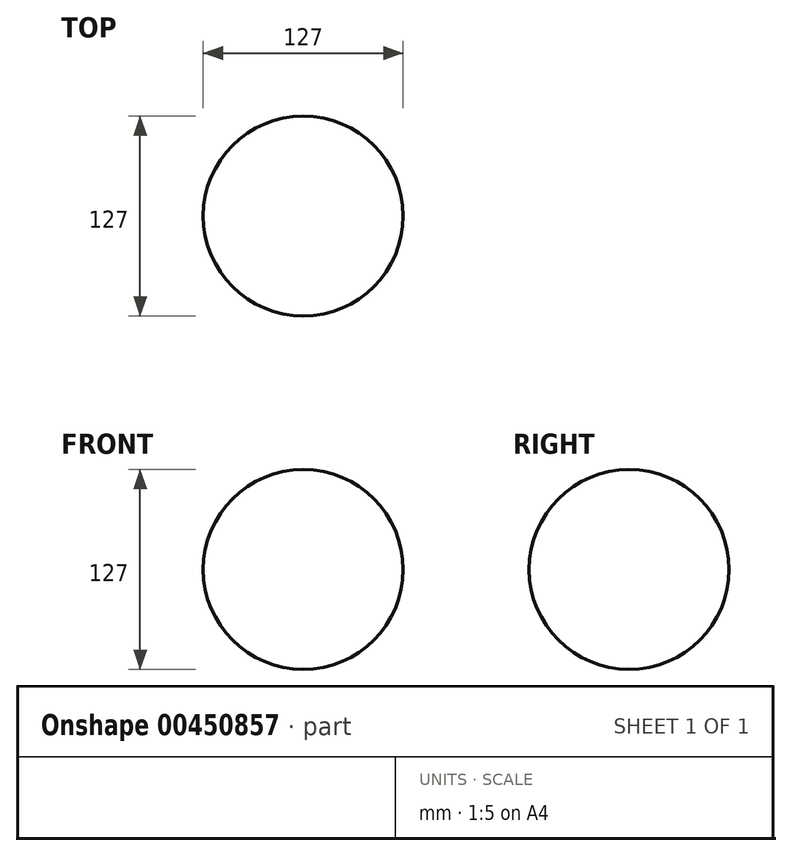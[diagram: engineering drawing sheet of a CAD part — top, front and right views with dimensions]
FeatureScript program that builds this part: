
annotation { "Feature Type Name" : "Feature", "Feature Type Description" : "" }
export const myFeature = defineFeature(function(context is Context, id is Id, definition is map)
    precondition{}
    {
        {
            var Q0;
            Q0=qCreatedBy(makeId("Right.planeOp"),FACE);
            var sketch = newSketch(context, id + "F0", { "sketchPlane" : qUnion([Q0])});
            skCircle(sketch, "E0", {"center": v(0, 0) * mm, "radius": 63.5 * mm});
            skLineSegment(sketch, "E1.bottom", {"start": v(-25.4, -93.12) * mm, "end": v(-38.1, -93.12) * mm});
            skLineSegment(sketch, "E1.top", {"start": v(-25.4, -58.2) * mm, "end": v(-38.1, -58.2) * mm});
            skLineSegment(sketch, "E1.left", {"start": v(-25.4, -93.12) * mm, "end": v(-25.4, -58.2) * mm});
            skLineSegment(sketch, "E1.right", {"start": v(-38.1, -93.12) * mm, "end": v(-38.1, -58.2) * mm});
            skLineSegment(sketch, "E2.MirrorCS", {"start": v(38.1, -93.12) * mm, "end": v(38.1, -58.2) * mm});
            skLineSegment(sketch, "E3.MirrorCS", {"start": v(25.4, -93.12) * mm, "end": v(25.4, -58.2) * mm});
            skLineSegment(sketch, "E4.MirrorCS", {"start": v(25.4, -93.12) * mm, "end": v(38.1, -93.12) * mm});
            skLineSegment(sketch, "E5.MirrorCS", {"start": v(25.4, -58.2) * mm, "end": v(38.1, -58.2) * mm});
            skLineSegment(sketch, "E6.bottom", {"start": v(-38.1, -93.12) * mm, "end": v(-50.8, -93.12) * mm});
            skLineSegment(sketch, "E6.top", {"start": v(-38.1, -50.8) * mm, "end": v(-50.8, -50.8) * mm});
            skLineSegment(sketch, "E6.left", {"start": v(-38.1, -93.12) * mm, "end": v(-38.1, -50.8) * mm});
            skLineSegment(sketch, "E6.right", {"start": v(-50.8, -93.12) * mm, "end": v(-50.8, -50.8) * mm});
            skLineSegment(sketch, "E7.MirrorCS", {"start": v(38.1, -93.12) * mm, "end": v(50.8, -93.12) * mm});
            skLineSegment(sketch, "E8.MirrorCS", {"start": v(50.8, -93.12) * mm, "end": v(50.8, -50.8) * mm});
            skLineSegment(sketch, "E9.MirrorCS", {"start": v(38.1, -93.12) * mm, "end": v(38.1, -50.8) * mm});
            skLineSegment(sketch, "E10.MirrorCS", {"start": v(38.1, -50.8) * mm, "end": v(50.8, -50.8) * mm});
            skLineSegment(sketch, "E11.bottom", {"start": v(25.4, 58.2) * mm, "end": v(50.8, 58.2) * mm});
            skLineSegment(sketch, "E11.top", {"start": v(25.4, 178.85) * mm, "end": v(50.8, 178.85) * mm});
            skLineSegment(sketch, "E11.left", {"start": v(25.4, 58.2) * mm, "end": v(25.4, 178.85) * mm});
            skLineSegment(sketch, "E11.right", {"start": v(50.8, 58.2) * mm, "end": v(50.8, 178.85) * mm});
            skPoint(sketch, "E12", {"position": v(25.4, 118.52) * mm});
            skLineSegment(sketch, "E13", {"start": v(0, 63.5) * mm, "end": v(0, -63.5) * mm});
            skSolve(sketch);
        }
        {
            var Q0;
            {var subQ4=sQuery(id+"F0.wireOp",EDGE,"E13");Q0=makeQuery(id+"F0.imprint","IMPRINT",FACE,{"disambiguationData":[TD([[makeQuery(id+"F0.imprint","IMPRINT",EDGE,{"derivedFrom":subQ4}),1.0]])]});}
            var Q1;
            Q1=sQuery(id+"F0.wireOp",EDGE,"E13");
            revolve(context, id + "F1", {"entities" : qUnion([Q0]), "axis" : qUnion([Q1]), "revolveType" : RevolveType.ONE_DIRECTION, "angle" : 360 * degree});
        }
    });
